# Revit family: SDD75X133
name_source: partatom
category: Detail Items
revit_build: Autodesk Revit 2015 (Build: 20140606_1530(x64)
units: mm (PartAtom-declared; Revit-internal decimal feet)

## types (2) — shared parameters
Density = 0.05 kg
Description = Self-Drilling Dowel
EPD = https://www.strongtie.eu
ETA / DoP = https://www.strongtie.eu
Manufacturer = Simpson Strong-Tie
Model = SDD7.5X133
Model Disclaimer = Contact Simpson Strong-Tie Company  for more information
Model ID = 0119470708918108315928591517815896633941
Name = SDD7.5X133
ObjectType = SDD7.5X133
Product Material = ElectroGalvanised
Product Type = Self-Drilling Dowel
Reference = 78121
Technical datasheet = https://www.strongtie.eu
URL = www.strongtie.eu
UniClass Number = Pr_20_29_76_76
UniClass Title = Self-drilling screws

## per-type parameters (varying)
| type | _visiblefront | _visibletop |
| SST_SDD7.5X133_Front | Yes | No |
| SST_SDD7.5X133_Top | No | Yes |

## geometry (parser evidence)
native form markers: Sweep x2
no freeform markers — native parametric forms only
